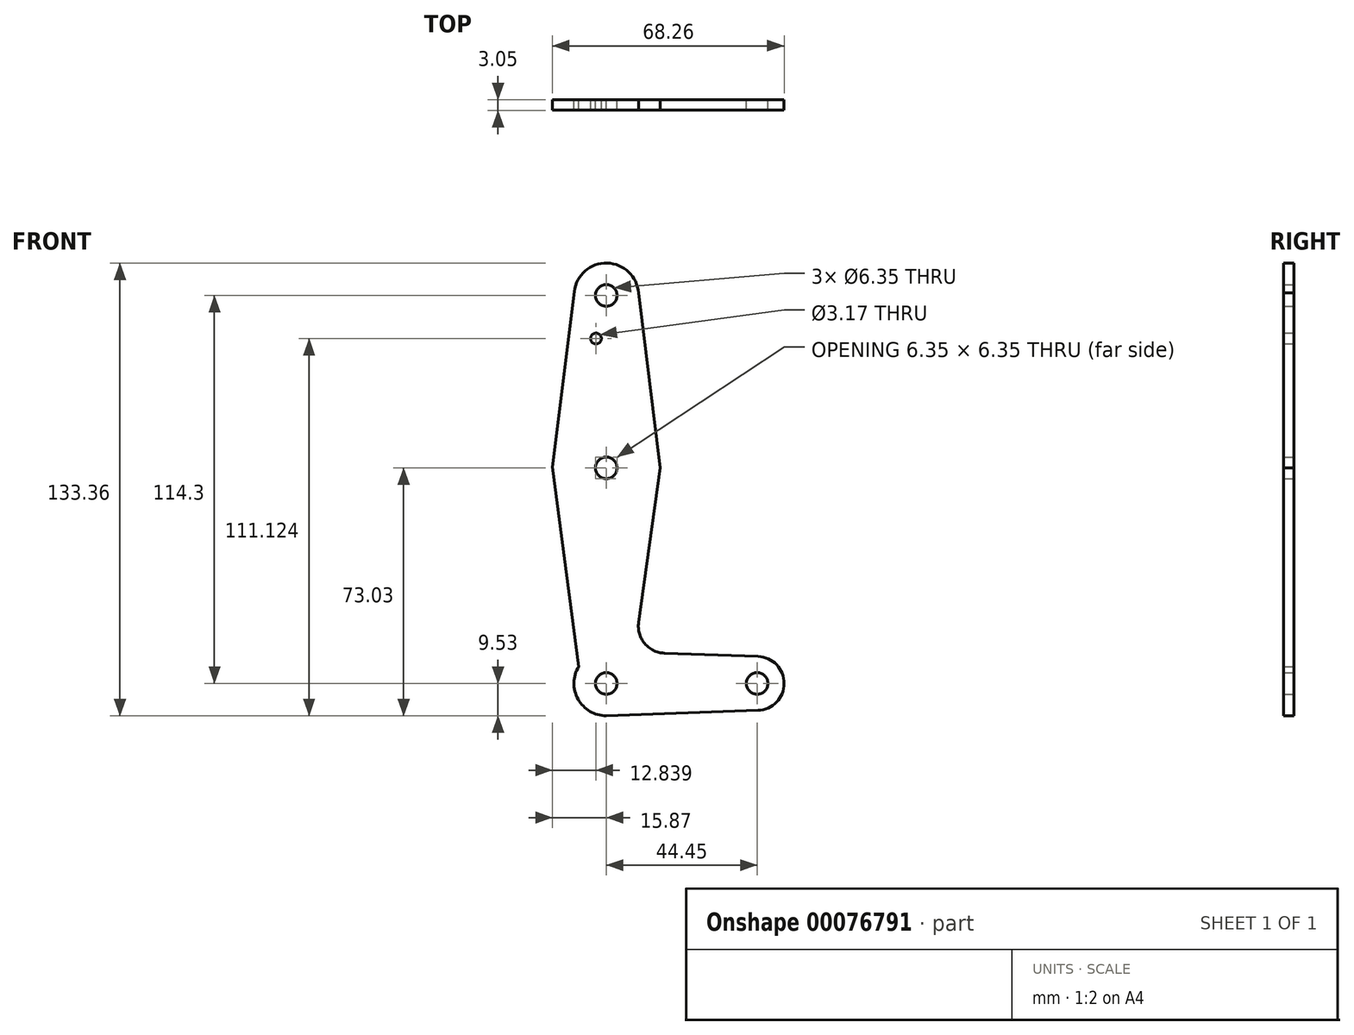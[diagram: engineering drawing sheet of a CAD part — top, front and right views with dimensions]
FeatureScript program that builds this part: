
annotation { "Feature Type Name" : "Feature", "Feature Type Description" : "" }
export const myFeature = defineFeature(function(context is Context, id is Id, definition is map)
    precondition{}
    {
        {
            var Q0;
            Q0=qCreatedBy(makeId("Front.planeOp"),FACE);
            var sketch = newSketch(context, id + "F0", { "sketchPlane" : qUnion([Q0])});
            skLineSegment(sketch, "E0", {"start": v(0, 0) * mm, "end": v(44.45, 0) * mm});
            skCircle(sketch, "E1", {"center": v(0, 114.3) * mm, "radius": 9.53 * mm});
            skCircle(sketch, "E2", {"center": v(0, 63.5) * mm, "radius": 15.88 * mm});
            skCircle(sketch, "E3", {"center": v(0, 0) * mm, "radius": 9.53 * mm});
            skCircle(sketch, "E4", {"center": v(44.45, 0) * mm, "radius": 7.94 * mm});
            skLineSegment(sketch, "E5", {"start": v(0, 114.3) * mm, "end": v(0, 0) * mm});
            skLineSegment(sketch, "E6", {"start": v(-15.87, 63.8) * mm, "end": v(-9.45, 115.47) * mm});
            skLineSegment(sketch, "E7", {"start": v(9.5, 115) * mm, "end": v(15.87, 63.44) * mm});
            skLineSegment(sketch, "E8", {"start": v(-15.87, 63.8) * mm, "end": v(-8.12, 4.98) * mm});
            skLineSegment(sketch, "E9", {"start": v(15.87, 63.44) * mm, "end": v(9.52, 17.96) * mm});
            skLineSegment(sketch, "E10", {"start": v(17.12, 8.92) * mm, "end": v(44.73, 7.93) * mm});
            skLineSegment(sketch, "E11", {"start": v(0, -9.52) * mm, "end": v(44.73, -7.93) * mm});
            skCircle(sketch, "E12", {"center": v(0, 114.3) * mm, "radius": 3.18 * mm});
            skCircle(sketch, "E13", {"center": v(0, 63.5) * mm, "radius": 3.18 * mm});
            skArc(sketch, "E14.filletArc", {"start": v(9.52, 17.96) * mm, "mid": v(11.3, 11.75) * mm, "end": v(17.12, 8.92) * mm});
            skCircle(sketch, "E15", {"center": v(0, 0) * mm, "radius": 3.18 * mm});
            skCircle(sketch, "E16", {"center": v(44.45, 0) * mm, "radius": 3.18 * mm});
            skCircle(sketch, "E17", {"center": v(-3.03, 101.6) * mm, "radius": 1.59 * mm});
            skSolve(sketch);
        }
        {
            var Q0;
            {var subQ1=sQuery(id+"F0.wireOp",EDGE,"E2");var subQ6=sQuery(id+"F0.wireOp",EDGE,"E6");var subQ8=makeQuery(id+"F0.imprint","INTERSECT",VERTEX,{"derivedFrom":[subQ1,subQ6]});Q0=makeQuery(id+"F0.imprint","IMPRINT",FACE,{"disambiguationData":[TD([[makeQuery(id+"F0.imprint","IMPRINT",EDGE,{"disambiguationData":[TD([[subQ8,1.0]])],"derivedFrom":subQ1}),1.0]])]});}
            var Q1;
            Q1=makeQuery(id+"F0.imprint","IMPRINT",FACE,{"disambiguationData":[TD([[makeQuery(id+"F0.imprint","IMPRINT",EDGE,{"derivedFrom":sQuery(id+"F0.wireOp",EDGE,"E17")}),-1.0]])]});
            var Q2;
            {var subQ0=sQuery(id+"F0.wireOp",EDGE,"E7");var subQ1=sQuery(id+"F0.wireOp",EDGE,"E1");var subQ2=makeQuery(id+"F0.imprint","INTERSECT",VERTEX,{"derivedFrom":[subQ1,subQ0]});Q2=makeQuery(id+"F0.imprint","IMPRINT",FACE,{"disambiguationData":[TD([[makeQuery(id+"F0.imprint","IMPRINT",EDGE,{"disambiguationData":[TD([[subQ2,1.0]])],"derivedFrom":subQ1}),-1.0]])]});}
            var Q3;
            Q3=makeQuery(id+"F0.imprint","IMPRINT",FACE,{"disambiguationData":[TD([[makeQuery(id+"F0.imprint","IMPRINT",EDGE,{"derivedFrom":sQuery(id+"F0.wireOp",EDGE,"E12")}),-1.0]])]});
            var Q4;
            {var subQ1=sQuery(id+"F0.wireOp",EDGE,"E2");var subQ9=sQuery(id+"F0.wireOp",EDGE,"E7");var subQ10=makeQuery(id+"F0.imprint","INTERSECT",VERTEX,{"derivedFrom":[subQ1,subQ9]});Q4=makeQuery(id+"F0.imprint","IMPRINT",FACE,{"disambiguationData":[TD([[makeQuery(id+"F0.imprint","IMPRINT",EDGE,{"disambiguationData":[TD([[subQ10,-1.0]])],"derivedFrom":subQ1}),1.0]])]});}
            var Q5;
            {var subQ0=sQuery(id+"F0.wireOp",EDGE,"E8");var subQ1=sQuery(id+"F0.wireOp",EDGE,"E2");var subQ2=makeQuery(id+"F0.imprint","INTERSECT",VERTEX,{"derivedFrom":[subQ1,subQ0]});Q5=makeQuery(id+"F0.imprint","IMPRINT",FACE,{"disambiguationData":[TD([[makeQuery(id+"F0.imprint","IMPRINT",EDGE,{"disambiguationData":[TD([[subQ2,-1.0]])],"derivedFrom":subQ1}),-1.0]])]});}
            var Q6;
            {var subQ0=sQuery(id+"F0.wireOp",EDGE,"E10");Q6=makeQuery(id+"F0.imprint","IMPRINT",FACE,{"disambiguationData":[TD([[makeQuery(id+"F0.imprint","IMPRINT",EDGE,{"derivedFrom":subQ0}),-1.0]])]});}
            var Q7;
            {var subQ0=sQuery(id+"F0.wireOp",EDGE,"E15");var subQ1=sQuery(id+"F0.wireOp",EDGE,"E0");var subQ2=makeQuery(id+"F0.imprint","INTERSECT",VERTEX,{"derivedFrom":[subQ1,subQ0]});Q7=makeQuery(id+"F0.imprint","IMPRINT",FACE,{"disambiguationData":[TD([[makeQuery(id+"F0.imprint","IMPRINT",EDGE,{"disambiguationData":[TD([[subQ2,-1.0]])],"derivedFrom":subQ1}),1.0]])]});}
            var Q8;
            {var subQ6=sQuery(id+"F0.wireOp",EDGE,"E0");var subQ8=sQuery(id+"F0.wireOp",EDGE,"E15");var subQ9=makeQuery(id+"F0.imprint","INTERSECT",VERTEX,{"derivedFrom":[subQ6,subQ8]});Q8=makeQuery(id+"F0.imprint","IMPRINT",FACE,{"disambiguationData":[TD([[makeQuery(id+"F0.imprint","IMPRINT",EDGE,{"disambiguationData":[TD([[subQ9,-1.0]])],"derivedFrom":subQ6}),-1.0]])]});}
            var Q9;
            {var subQ0=sQuery(id+"F0.wireOp",EDGE,"E4");var subQ1=sQuery(id+"F0.wireOp",EDGE,"E0");var subQ2=makeQuery(id+"F0.imprint","INTERSECT",VERTEX,{"derivedFrom":[subQ1,subQ0]});Q9=makeQuery(id+"F0.imprint","IMPRINT",FACE,{"disambiguationData":[TD([[makeQuery(id+"F0.imprint","IMPRINT",EDGE,{"disambiguationData":[TD([[subQ2,1.0]])],"derivedFrom":subQ1}),-1.0]])]});}
            var Q10;
            Q10=makeQuery(id+"F0.imprint","IMPRINT",FACE,{"disambiguationData":[TD([[makeQuery(id+"F0.imprint","IMPRINT",EDGE,{"derivedFrom":sQuery(id+"F0.wireOp",EDGE,"E16")}),-1.0]])]});
            extrude(context, id + "F1", {"entities" : qUnion([Q0, Q1, Q2, Q3, Q4, Q5, Q6, Q7, Q8, Q9, Q10]), "depth" : 3.05 * mm});
        }
    });
